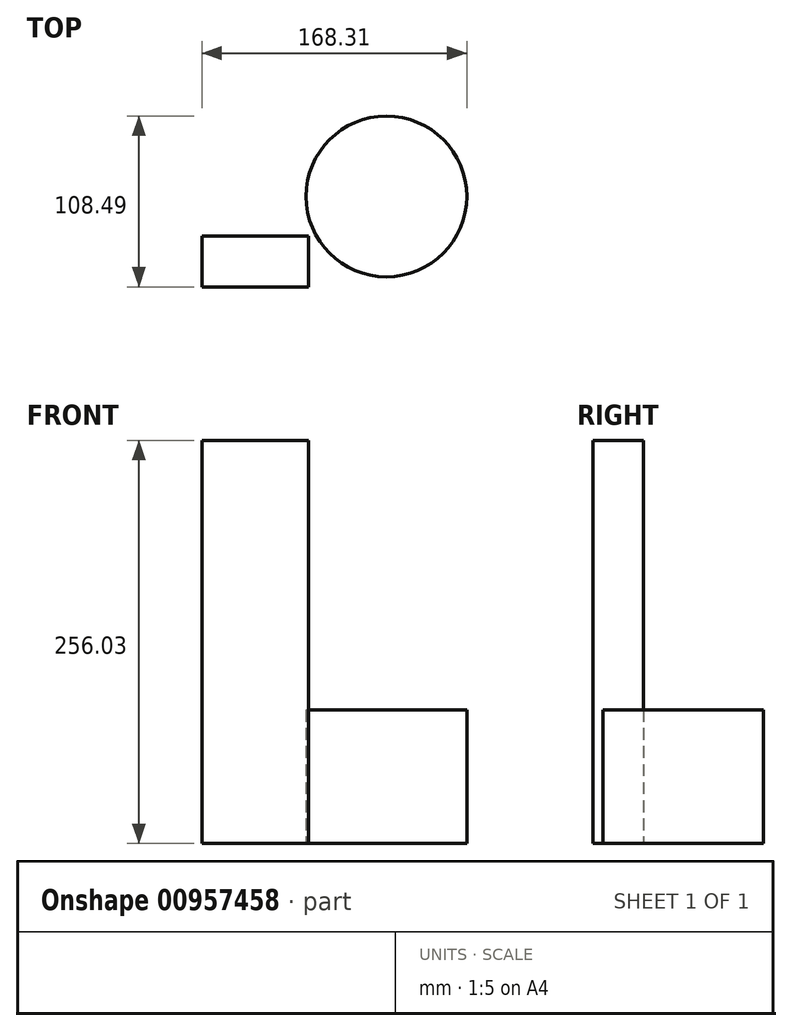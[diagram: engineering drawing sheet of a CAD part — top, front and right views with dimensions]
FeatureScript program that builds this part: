
annotation { "Feature Type Name" : "Feature", "Feature Type Description" : "" }
export const myFeature = defineFeature(function(context is Context, id is Id, definition is map)
    precondition{}
    {
        {
            var Q0;
            Q0=qCreatedBy(makeId("Top.planeOp"),FACE);
            var sketch = newSketch(context, id + "F0", { "sketchPlane" : qUnion([Q0])});
            skCircle(sketch, "E0", {"center": v(0, 0) * mm, "radius": 51.06 * mm});
            skSolve(sketch);
        }
        {
            var Q0;
            Q0=makeQuery(id+"F0.imprint","IMPRINT",FACE,{"disambiguationData":[TD([[makeQuery(id+"F0.imprint","IMPRINT",EDGE,{"derivedFrom":sQuery(id+"F0.wireOp",EDGE,"E0")}),1.0]])]});
            extrude(context, id + "F1", {"entities" : qUnion([Q0]), "depth" : 84.84 * mm, "offsetDistance" : 25.4 * mm});
        }
        {
            var Q0;
            Q0=qCreatedBy(makeId("Top.planeOp"),FACE);
            var sketch = newSketch(context, id + "F2", { "sketchPlane" : qUnion([Q0])});
            skLineSegment(sketch, "E1.bottom", {"start": v(-117.25, -57.43) * mm, "end": v(-49.44, -57.43) * mm});
            skLineSegment(sketch, "E1.top", {"start": v(-117.25, -25.19) * mm, "end": v(-49.44, -25.19) * mm});
            skLineSegment(sketch, "E1.left", {"start": v(-117.25, -57.43) * mm, "end": v(-117.25, -25.19) * mm});
            skLineSegment(sketch, "E1.right", {"start": v(-49.44, -57.43) * mm, "end": v(-49.44, -25.19) * mm});
            skSolve(sketch);
        }
        {
            var Q0;
            Q0=makeQuery(id+"F2.imprint","IMPRINT",FACE,{"disambiguationData":[TD([[makeQuery(id+"F2.imprint","IMPRINT",EDGE,{"derivedFrom":sQuery(id+"F2.wireOp",EDGE,"E1.bottom")}),1.0]])]});
            extrude(context, id + "F3", {"entities" : qUnion([Q0]), "depth" : 256.03 * mm, "offsetDistance" : 25.4 * mm});
        }
    });
